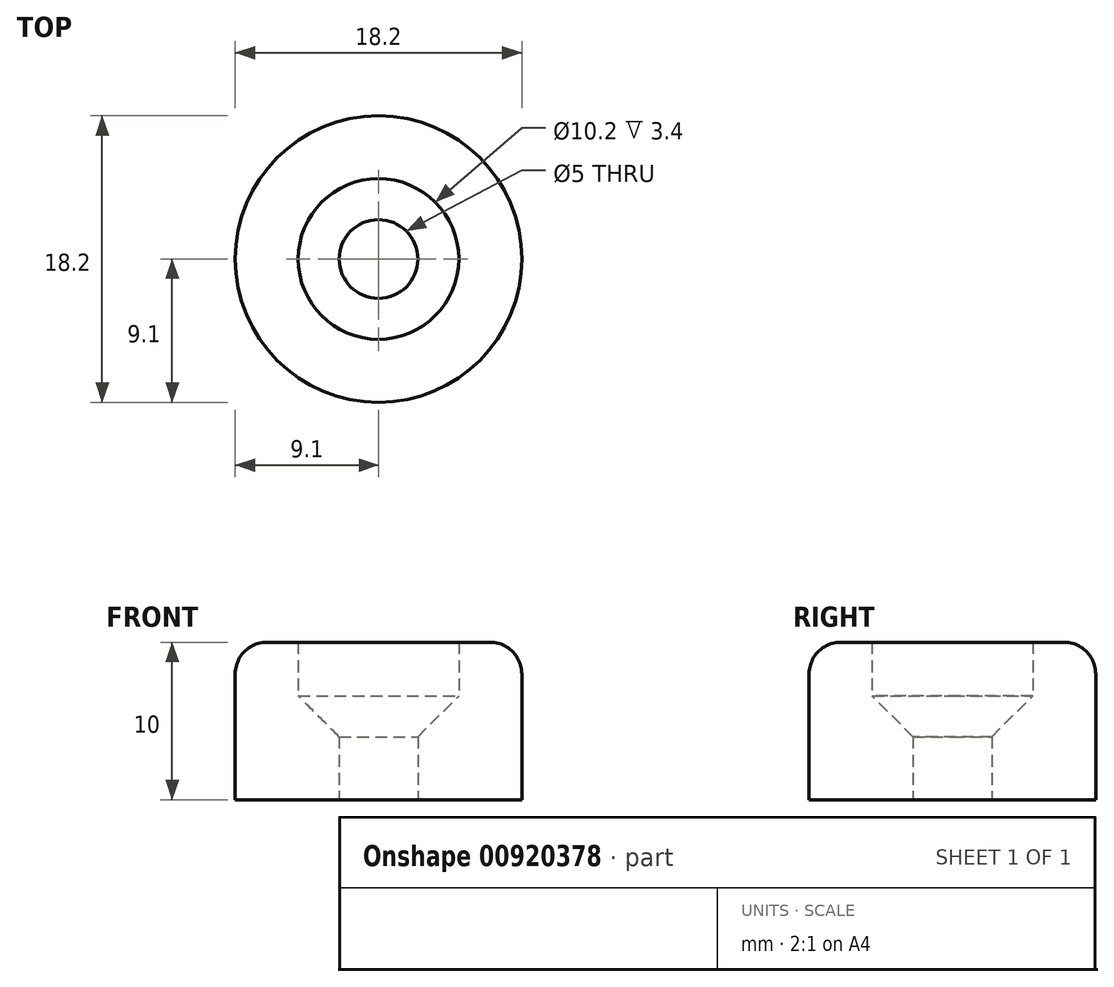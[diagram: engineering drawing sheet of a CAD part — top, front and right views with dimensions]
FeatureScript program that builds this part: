
annotation { "Feature Type Name" : "Feature", "Feature Type Description" : "" }
export const myFeature = defineFeature(function(context is Context, id is Id, definition is map)
    precondition{}
    {
        {
            var Q0;
            Q0=qCreatedBy(makeId("Right.planeOp"),FACE);
            var sketch = newSketch(context, id + "F0", { "sketchPlane" : qUnion([Q0])});
            skLineSegment(sketch, "E0", {"start": v(-2.5, 0) * mm, "end": v(-9.1, 0) * mm});
            skLineSegment(sketch, "E1", {"start": v(-9.1, 0) * mm, "end": v(-9.1, 8) * mm});
            skLineSegment(sketch, "E2", {"start": v(-7.1, 10) * mm, "end": v(-5.1, 10) * mm});
            skLineSegment(sketch, "E3", {"start": v(-5.1, 10) * mm, "end": v(-5.1, 6.6) * mm});
            skLineSegment(sketch, "E4", {"start": v(-5.1, 6.6) * mm, "end": v(-2.5, 4) * mm});
            skLineSegment(sketch, "E5", {"start": v(-2.5, 4) * mm, "end": v(-2.5, 0) * mm});
            skPoint(sketch, "E6.visualSharp", {"position": v(-9.1, 10) * mm});
            skArc(sketch, "E6.filletArc", {"start": v(-7.1, 10) * mm, "mid": v(-8.51, 9.41) * mm, "end": v(-9.1, 8) * mm});
            skPoint(sketch, "E7.orphan", {"position": v(0, 0) * mm});
            skLineSegment(sketch, "E8", {"start": v(0, 0) * mm, "end": v(0, 12.13) * mm});
            skSolve(sketch);
        }
        {
            var Q0;
            Q0=makeQuery(id+"F0.imprint","IMPRINT",FACE,{"disambiguationData":[TD([[makeQuery(id+"F0.imprint","IMPRINT",EDGE,{"derivedFrom":sQuery(id+"F0.wireOp",EDGE,"E0")}),-1.0]])]});
            var Q1;
            Q1=sQuery(id+"F0.wireOp",EDGE,"E8");
            revolve(context, id + "F1", {"surfaceOperationType" : NewSurfaceOperationType.NEW, "entities" : qUnion([Q0]), "axis" : qUnion([Q1]), "revolveType" : RevolveType.FULL});
        }
    });
